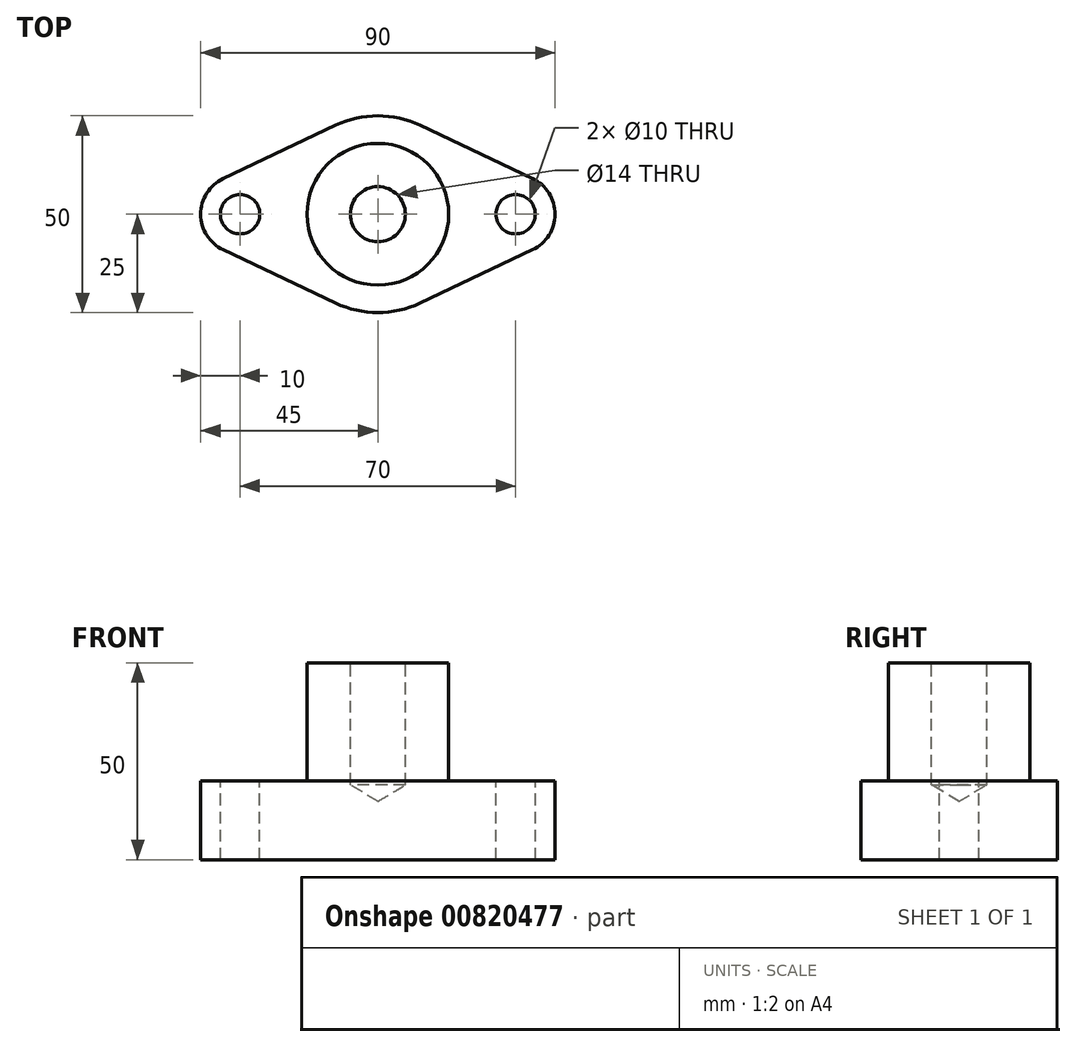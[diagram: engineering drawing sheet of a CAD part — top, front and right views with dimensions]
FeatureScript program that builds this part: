
annotation { "Feature Type Name" : "Feature", "Feature Type Description" : "" }
export const myFeature = defineFeature(function(context is Context, id is Id, definition is map)
    precondition{}
    {
        {
            var Q0;
            Q0=qCreatedBy(makeId("Top.planeOp"),FACE);
            var sketch = newSketch(context, id + "F0", { "sketchPlane" : qUnion([Q0])});
            skLineSegment(sketch, "E0", {"start": v(-39.29, 9.04) * mm, "end": v(-10.71, 22.59) * mm});
            skLineSegment(sketch, "E1", {"start": v(-39.29, -9.04) * mm, "end": v(-10.71, -22.59) * mm});
            skLineSegment(sketch, "E2", {"start": v(39.29, -9.04) * mm, "end": v(10.71, -22.59) * mm});
            skLineSegment(sketch, "E3", {"start": v(10.71, 22.59) * mm, "end": v(10.71, 22.59) * mm});
            skArc(sketch, "E4", {"start": v(-39.29, 9.04) * mm, "mid": v(-45, 0) * mm, "end": v(-39.29, -9.04) * mm});
            skArc(sketch, "E5", {"start": v(-10.71, -22.59) * mm, "mid": v(0, -25) * mm, "end": v(10.71, -22.59) * mm});
            skLineSegment(sketch, "E6", {"start": v(10.71, -22.59) * mm, "end": v(10.71, -22.59) * mm});
            skLineSegment(sketch, "E7", {"start": v(10.71, 22.59) * mm, "end": v(39.29, 9.04) * mm});
            skArc(sketch, "E8", {"start": v(10.71, 22.59) * mm, "mid": v(0, 25) * mm, "end": v(-10.71, 22.59) * mm});
            skArc(sketch, "E9", {"start": v(39.29, -9.04) * mm, "mid": v(45, 0) * mm, "end": v(39.29, 9.04) * mm});
            skSolve(sketch);
        }
        {
            var Q0;
            Q0=makeQuery(id+"F0.imprint","IMPRINT",FACE,{"disambiguationData":[TD([[makeQuery(id+"F0.imprint","IMPRINT",EDGE,{"derivedFrom":sQuery(id+"F0.wireOp",EDGE,"E0")}),-1.0]])]});
            extrude(context, id + "F1", {"entities" : qUnion([Q0]), "depth" : 20 * mm, "offsetDistance" : 25 * mm});
        }
        {
            var Q0;
            Q0=makeQuery(id+"F1.opExtrude","CAP_FACE",FACE,{"disambiguationData":[OSD([sQuery(id+"F0.wireOp",EDGE,"E0"),sQuery(id+"F0.wireOp",EDGE,"E1"),sQuery(id+"F0.wireOp",EDGE,"E2"),sQuery(id+"F0.wireOp",EDGE,"E4"),sQuery(id+"F0.wireOp",EDGE,"E5"),sQuery(id+"F0.wireOp",EDGE,"E7"),sQuery(id+"F0.wireOp",EDGE,"E8"),sQuery(id+"F0.wireOp",EDGE,"E9")])],"isStart":false});
            var sketch = newSketch(context, id + "F2", { "sketchPlane" : qUnion([Q0])});
            skPoint(sketch, "E10", {"position": v(-35, 0) * mm});
            skPoint(sketch, "E11", {"position": v(35, 0) * mm});
            skCircle(sketch, "E12", {"center": v(0, 0) * mm, "radius": 18 * mm});
            skSolve(sketch);
        }
        {
            var Q0;
            Q0=makeQuery(id+"F2.imprint","IMPRINT",FACE,{"disambiguationData":[TD([[makeQuery(id+"F2.imprint","IMPRINT",EDGE,{"derivedFrom":sQuery(id+"F2.wireOp",EDGE,"E12")}),1.0]])]});
            extrude(context, id + "F3", {"entities" : qUnion([Q0]), "operationType" : NewBodyOperationType.ADD, "depth" : 30 * mm, "offsetDistance" : 25 * mm});
        }
        {
            var Q0;
            Q0=sQuery(id+"F2.wireOp",VERTEX,"E10");
            var Q1;
            Q1=sQuery(id+"F2.wireOp",VERTEX,"E11");
            var Q2;
            Q2=makeQuery(id+"F1.opExtrude","SWEPT_BODY",BODY,{"disambiguationData":[OSD([sQuery(id+"F0.wireOp",EDGE,"E0"),sQuery(id+"F0.wireOp",EDGE,"E1"),sQuery(id+"F0.wireOp",EDGE,"E2"),sQuery(id+"F0.wireOp",EDGE,"E4"),sQuery(id+"F0.wireOp",EDGE,"E5"),sQuery(id+"F0.wireOp",EDGE,"E7"),sQuery(id+"F0.wireOp",EDGE,"E8"),sQuery(id+"F0.wireOp",EDGE,"E9")])]});
            hole(context, id + "F4", {"style" : HoleStyle.SIMPLE, "endStyle" : HoleEndStyle.THROUGH, "holeDiameter" : 10 * mm, "majorDiameter" : 5 * mm, "isTappedThrough" : true, "tappedDepth" : 12 * mm, "tapClearance" : 3, "locations" : qUnion([Q0, Q1]), "scope" : qUnion([Q2])});
        }
        {
            var Q0;
            Q0=makeQuery(id+"F3.opExtrude","CAP_FACE",FACE,{"disambiguationData":[OSD([sQuery(id+"F2.wireOp",EDGE,"E12")])],"isStart":false});
            var sketch = newSketch(context, id + "F5", { "sketchPlane" : qUnion([Q0])});
            skPoint(sketch, "E13", {"position": v(0, 0) * mm});
            skSolve(sketch);
        }
        {
            var Q0;
            Q0=sQuery(id+"F5.wireOp",VERTEX,"E13");
            var Q1;
            Q1=makeQuery(id+"F1.opExtrude","SWEPT_BODY",BODY,{"disambiguationData":[OSD([sQuery(id+"F0.wireOp",EDGE,"E0"),sQuery(id+"F0.wireOp",EDGE,"E1"),sQuery(id+"F0.wireOp",EDGE,"E2"),sQuery(id+"F0.wireOp",EDGE,"E4"),sQuery(id+"F0.wireOp",EDGE,"E5"),sQuery(id+"F0.wireOp",EDGE,"E7"),sQuery(id+"F0.wireOp",EDGE,"E8"),sQuery(id+"F0.wireOp",EDGE,"E9")])]});
            hole(context, id + "F6", {"style" : HoleStyle.SIMPLE, "endStyle" : HoleEndStyle.BLIND, "standardTappedOrClearance" : lookupTablePath({ "standard" : "ISO", "engagement" : "75%", "pitch" : "2 mm", "size" : "M16", "type" : "Tapped" }), "standardBlindInLast" : lookupTablePath({ "standard" : "ISO", "engagement" : "75%", "pitch" : "2 mm", "size" : "M16", "type" : "Tapped" }), "holeDiameter" : 14 * mm, "majorDiameter" : 16 * mm, "showTappedDepth" : true, "holeDepth" : 31 * mm, "isTappedThrough" : true, "tappedDepth" : 25 * mm, "tapClearance" : 3, "locations" : qUnion([Q0]), "scope" : qUnion([Q1])});
        }
    });
